# Revit family: QUADROP-TR-xxFSWxxxM0225
name_source: partatom
category: Oprawy oświetleniowe
units: mm (PartAtom-declared; Revit-internal decimal feet)

## family parameters
Numer OmniClass = 23.80.70.11
Obiekt nadrzędny = Powierzchnia
Punkt obliczania pomieszczeń = Nie
Tnij formami wycięć po wczytaniu = Nie
Typ części = Normalny
Tytuł OmniClass = Luminaries for Internal Lighting
Współdzielony = Nie
Wymiar okrągłego złącza = Użyj średnicy
Źródło światła = Tak

## types (4) — shared parameters
Emituj kształt widoczny w renderingu = Nie
Emituj z długości prostokąta = 78 mm  [stored 0.255906 ft]
Emituj z szerokości prostokąta = 78 mm  [stored 0.255906 ft]
Filtr koloru = 16777215
Kod zespołu = D5020200
Lampa = LED
Obciążenie pozorne = 27 VA
Odchylenie kierunku = 90.00°
Plik sieci fotometrycznej = QUADROP-S DAFSW840M0200.IES
Producent = RIDI Leuchten GmbH
URL = www.spectral.de
Zmiana temperatury barwowej przyciemniania lampy = <Brak>
brand = Spectral
conformity mark = CE
electrical safety class = 1
height = 47 mm  [stored 0.154199 ft]
ingress protection (IP) code = IP20
length = 150 mm
nominal frequency = 50-60Hz
nominal voltage = 230
rated input power = 27
voltage type (AC, DC, UC) = AC
weight = 1,1 kg
width = 150 mm
zero-valued in all types: Domyślna rzędna

## per-type parameters (varying)
| type | Model |
| QUADROP-TR NDFSW830M0225 | SPG0320252AQ |
| QUADROP-TR DAFSW830M0225 | SPG0330252AQ |
| QUADROP-TR NDFSW840M0225 | SPG0320255AQ |
| QUADROP-TR DAFSW840M0225 | SPG0330255AQ |

note: column(s) folded — value = type name in every type: product name

note: [stored X ft] marks values corroborated as IEEE doubles in the binary element streams (Revit-internal decimal feet)
